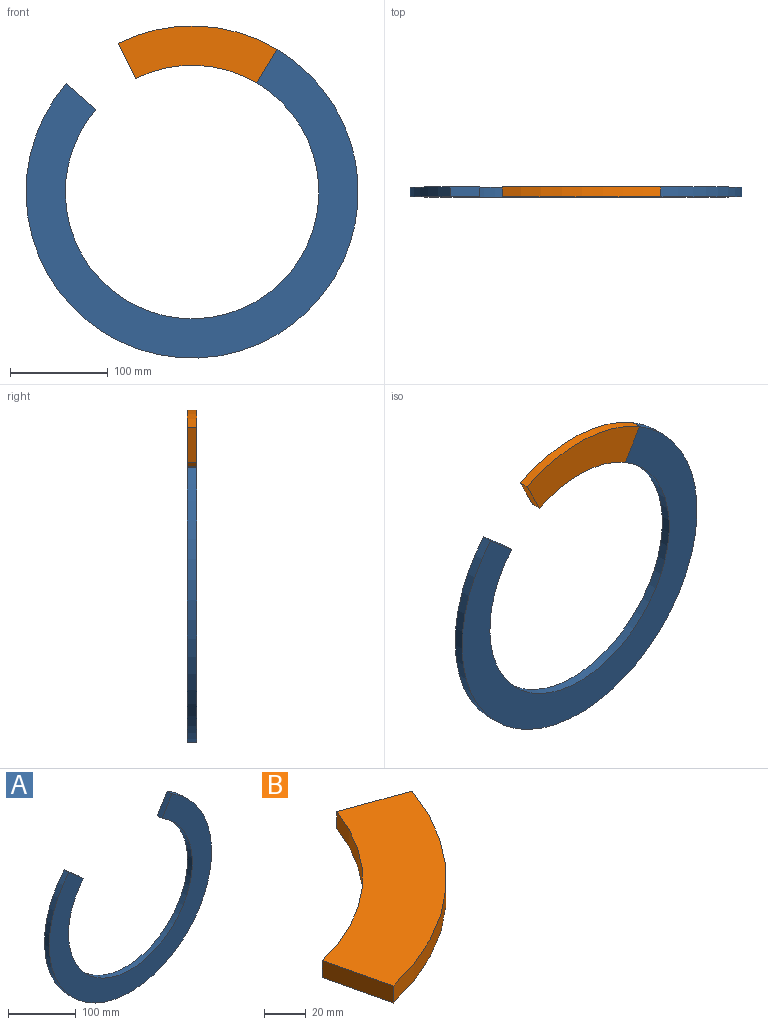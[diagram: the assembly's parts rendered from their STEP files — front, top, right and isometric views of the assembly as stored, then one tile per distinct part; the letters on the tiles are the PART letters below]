
ASSEMBLY  parts=2 mates=1
PART A: 6 faces, bbox 340x10x316.2 mm
  f0: cylinder r=129.75mm len=259.5mm, axis (0,1,0), area 6340.8mm2, adj f1,f3,f4,f5
  f1: plane 30.51x26.25mm, normal (0.65,0,0.76), area 402.5mm2, adj f0,f2,f4,f5
  f2: cylinder r=170mm len=340mm, axis (0,1,0), area 8307.8mm2, adj f1,f3,f4,f5
  f3: plane 34.61x20.55mm, normal (-0.86,0,0.51), area 402.5mm2, adj f0,f2,f4,f5
  f4: plane 340x316.17mm, normal (0,-1,0), area 29480.2mm2, adj f0,f1,f2,f3
  f5: plane 340x316.17mm, normal (0,1,0), area 29480.2mm2, adj f0,f1,f2,f3
PART B: 6 faces, bbox 130.5x122x10 mm
  f0: cylinder r=170mm len=121.32mm, axis (0,0,-1), area 1696.8mm2, adj f1,f3,f4,f5
  f1: plane 37.91x13.51mm, normal (0.34,0.94,0), area 402.5mm2, adj f0,f2,f4,f5
  f2: cylinder r=129.75mm len=92.6mm, axis (0,0,-1), area 1295.1mm2, adj f1,f3,f4,f5
  f3: plane 39.19x10mm, normal (-0.97,-0.23,0), area 402.5mm2, adj f0,f2,f4,f5
  f4: plane 130.51x121.96mm, normal (0,0,1), area 6021.2mm2, adj f0,f1,f2,f3
  f5: plane 130.51x121.96mm, normal (0,0,-1), area 6021.2mm2, adj f0,f1,f2,f3
PLACE A t=(-12.28,-7.47,3.85)mm fixed
PLACE B rot(axis=(-0.89,-0.32,-0.32),96.6deg) t=(-12.28,-17.47,3.85)mm
MATE fastened B.f1 <-> A.f3  axis (0.86,0,-0.51) through (64.25,-7.47,132.71)mm
